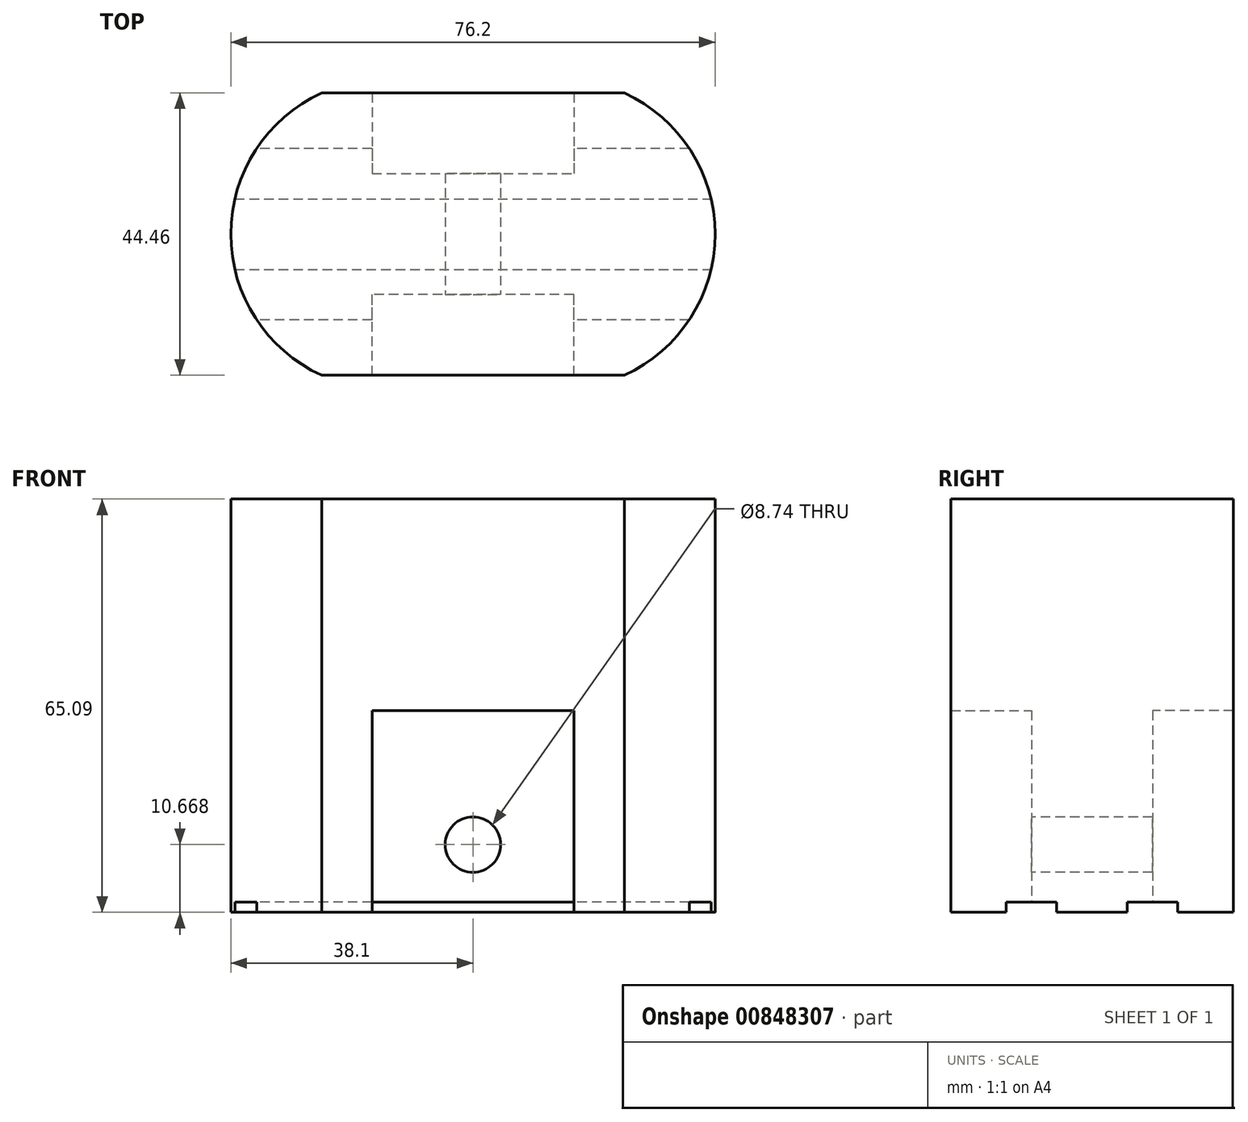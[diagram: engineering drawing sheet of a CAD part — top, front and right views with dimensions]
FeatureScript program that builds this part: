
annotation { "Feature Type Name" : "Feature", "Feature Type Description" : "" }
export const myFeature = defineFeature(function(context is Context, id is Id, definition is map)
    precondition{}
    {
        {
            var Q0;
            Q0=qCreatedBy(makeId("Top.planeOp"),FACE);
            var sketch = newSketch(context, id + "F0", { "sketchPlane" : qUnion([Q0])});
            skLineSegment(sketch, "E0.bottom", {"start": v(-23.81, -22.23) * mm, "end": v(23.81, -22.23) * mm});
            skLineSegment(sketch, "E0.top", {"start": v(-23.81, 22.22) * mm, "end": v(23.81, 22.22) * mm});
            skPoint(sketch, "E0.middle", {"position": v(0, 0) * mm});
            skPoint(sketch, "E1", {"position": v(-38.1, 0) * mm});
            skPoint(sketch, "E2", {"position": v(-23.81, 22.22) * mm});
            skPoint(sketch, "E3", {"position": v(-23.81, -22.23) * mm});
            skArc(sketch, "E4", {"start": v(-23.81, 22.22) * mm, "mid": v(-38.1, 0) * mm, "end": v(-23.81, -22.23) * mm});
            skArc(sketch, "E5.MirrorCS", {"start": v(23.81, 22.22) * mm, "mid": v(38.1, 0) * mm, "end": v(23.81, -22.23) * mm});
            skPoint(sketch, "E6.orphan", {"position": v(-38.1, 22.22) * mm});
            skPoint(sketch, "E7.orphan", {"position": v(-38.1, -22.23) * mm});
            skPoint(sketch, "E8.orphan", {"position": v(38.1, 22.22) * mm});
            skPoint(sketch, "E9.orphan", {"position": v(38.1, -22.23) * mm});
            skPoint(sketch, "E10", {"position": v(38.1, 0) * mm});
            skSolve(sketch);
        }
        {
            var Q0;
            Q0 = qSketchRegion(id + "F0", true);
            extrude(context, id + "F1", {"entities" : qUnion([Q0]), "depth" : 65.1 * mm, "offsetDistance" : 25.4 * mm});
        }
        {
            var Q0;
            Q0=makeQuery(id+"F1.opExtrude","CAP_FACE",FACE,{"disambiguationData":[OSD([sQuery(id+"F0.wireOp",EDGE,"E0.bottom"),sQuery(id+"F0.wireOp",EDGE,"E0.top"),sQuery(id+"F0.wireOp",EDGE,"E4"),sQuery(id+"F0.wireOp",EDGE,"E5.MirrorCS")])],"isStart":true});
            var sketch = newSketch(context, id + "F2", { "sketchPlane" : qUnion([Q0])});
            skLineSegment(sketch, "E11.0", {"start": v(-23.81, 22.23) * mm, "end": v(23.81, 22.23) * mm});
            skLineSegment(sketch, "E12.0", {"start": v(-23.81, -22.22) * mm, "end": v(23.81, -22.22) * mm});
            skPoint(sketch, "E13", {"position": v(0, 22.23) * mm});
            skLineSegment(sketch, "E14", {"start": v(-15.88, 22.23) * mm, "end": v(-15.88, 9.53) * mm});
            skLineSegment(sketch, "E15", {"start": v(-15.88, 9.53) * mm, "end": v(0, 9.53) * mm});
            skLineSegment(sketch, "E16.MirrorCS", {"start": v(15.88, 22.23) * mm, "end": v(15.88, 9.53) * mm});
            skLineSegment(sketch, "E17.MirrorCS", {"start": v(15.88, 9.53) * mm, "end": v(0, 9.53) * mm});
            skLineSegment(sketch, "E18.MirrorCS", {"start": v(-15.88, -22.23) * mm, "end": v(-15.88, -9.53) * mm});
            skLineSegment(sketch, "E19.MirrorCS", {"start": v(-15.88, -9.53) * mm, "end": v(0, -9.53) * mm});
            skLineSegment(sketch, "E20.MirrorCS", {"start": v(15.88, -9.53) * mm, "end": v(0, -9.53) * mm});
            skLineSegment(sketch, "E21.MirrorCS", {"start": v(15.88, -22.23) * mm, "end": v(15.88, -9.53) * mm});
            skLineSegment(sketch, "E22", {"start": v(-40.73, 0) * mm, "end": v(40.38, 0) * mm, "construction": true});
            skLineSegment(sketch, "E23", {"start": v(-37.46, 5.56) * mm, "end": v(37.46, 5.56) * mm});
            skLineSegment(sketch, "E24", {"start": v(34.04, 13.5) * mm, "end": v(-34.04, 13.5) * mm});
            skLineSegment(sketch, "E25.MirrorCS", {"start": v(-37.46, -5.56) * mm, "end": v(37.46, -5.56) * mm});
            skLineSegment(sketch, "E26.MirrorCS", {"start": v(34.04, -13.5) * mm, "end": v(-34.04, -13.5) * mm});
            skSolve(sketch);
        }
        {
            var Q0;
            Q0 = qSketchRegion(id + "F2", true);
            extrude(context, id + "F3", {"entities" : qUnion([Q0]), "operationType" : NewBodyOperationType.REMOVE, "oppositeDirection" : true, "depth" : 31.75 * mm, "offsetDistance" : 25.4 * mm});
        }
        {
            var Q0;
            {var subQ11=sQuery(id+"F2.wireOp",EDGE,"E15");Q0=makeQuery(id+"F2.imprint","IMPRINT",FACE,{"disambiguationData":[TD([[makeQuery(id+"F2.imprint","IMPRINT",EDGE,{"derivedFrom":subQ11}),-1.0]])]});}
            var Q1;
            {var subQ4=sQuery(id+"F2.wireOp",EDGE,"E19.MirrorCS");Q1=makeQuery(id+"F2.imprint","IMPRINT",FACE,{"disambiguationData":[TD([[makeQuery(id+"F2.imprint","IMPRINT",EDGE,{"derivedFrom":subQ4}),1.0]])]});}
            extrude(context, id + "F4", {"entities" : qUnion([Q0, Q1]), "operationType" : NewBodyOperationType.REMOVE, "oppositeDirection" : true, "depth" : 1.59 * mm, "offsetDistance" : 25.4 * mm});
        }
        {
            var Q0;
            Q0=makeQuery(id+"F3.boolean.opBoolean","COPY",FACE,{"derivedFrom":makeQuery(id+"F3.opExtrude","SWEPT_FACE",FACE,{"disambiguationData":[OSD([sQuery(id+"F2.wireOp",EDGE,"E15"),sQuery(id+"F2.wireOp",EDGE,"E17.MirrorCS")])]})});
            var sketch = newSketch(context, id + "F5", { "sketchPlane" : qUnion([Q0])});
            skLineSegment(sketch, "E27.0.0", {"start": v(-15.87, 1.59) * mm, "end": v(15.88, 1.59) * mm});
            skLineSegment(sketch, "E27.0.1", {"start": v(15.88, 1.59) * mm, "end": v(15.88, 31.75) * mm});
            skLineSegment(sketch, "E27.0.2", {"start": v(15.88, 31.75) * mm, "end": v(-15.87, 31.75) * mm});
            skLineSegment(sketch, "E27.0.3", {"start": v(-15.87, 31.75) * mm, "end": v(-15.87, 1.59) * mm});
            skLineSegment(sketch, "E28.0", {"start": v(-37.46, 0) * mm, "end": v(37.46, 0) * mm});
            skPoint(sketch, "E29", {"position": v(0, 10.67) * mm});
            skPoint(sketch, "E29.positionSnap0", {"position": v(0, 1.59) * mm});
            skSolve(sketch);
        }
        {
            var Q0;
            Q0=sQuery(id+"F5.wireOp",VERTEX,"E29");
            var Q1;
            Q1=makeQuery(id+"F1.opExtrude","SWEPT_BODY",BODY,{"disambiguationData":[OSD([sQuery(id+"F0.wireOp",EDGE,"E0.bottom"),sQuery(id+"F0.wireOp",EDGE,"E0.top"),sQuery(id+"F0.wireOp",EDGE,"E4"),sQuery(id+"F0.wireOp",EDGE,"E5.MirrorCS")])]});
            hole(context, id + "F6", {"style" : HoleStyle.SIMPLE, "endStyle" : HoleEndStyle.THROUGH, "standardTappedOrClearance" : lookupTablePath({ "fit" : "Normal (ASME)", "standard" : "ANSI", "size" : "5/16", "type" : "Clearance" }), "standardBlindInLast" : lookupTablePath({ "fit" : "Normal", "standard" : "ANSI", "engagement" : "75%", "pitch" : "18 tpi", "size" : "5/16", "type" : "Clearance & tapped" }), "holeDiameter" : 8.74 * mm, "majorDiameter" : 11.1 * mm, "isTappedThrough" : true, "tappedDepth" : 22.22 * mm, "tapClearance" : 3, "locations" : qUnion([Q0]), "scope" : qUnion([Q1])});
        }
    });
